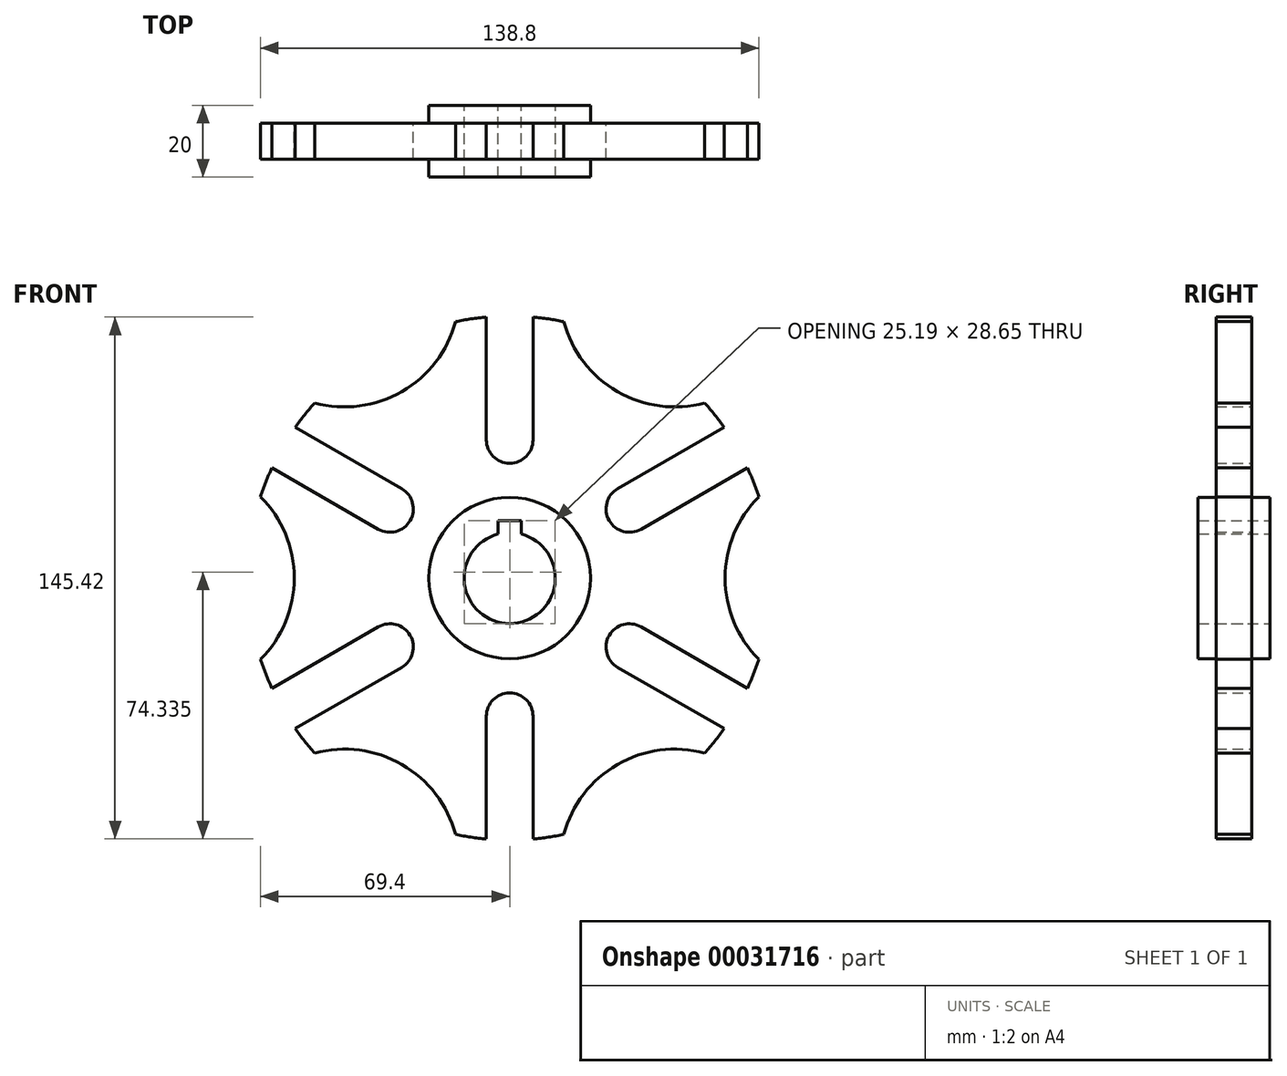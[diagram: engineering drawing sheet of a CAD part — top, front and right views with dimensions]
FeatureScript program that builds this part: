
annotation { "Feature Type Name" : "Feature", "Feature Type Description" : "" }
export const myFeature = defineFeature(function(context is Context, id is Id, definition is map)
    precondition{}
    {
        {
            var Q0;
            Q0=qCreatedBy(makeId("Front.planeOp"),FACE);
            var sketch = newSketch(context, id + "F0", { "sketchPlane" : qUnion([Q0])});
            skCircle(sketch, "E0", {"center": v(0, 0) * mm, "radius": 22.5 * mm});
            skCircle(sketch, "E1", {"center": v(0, 0) * mm, "radius": 12.7 * mm});
            skLineSegment(sketch, "E2", {"start": v(0, 12.7) * mm, "end": v(0, 15.95) * mm});
            skLineSegment(sketch, "E3", {"start": v(0, 15.95) * mm, "end": v(3.25, 15.95) * mm});
            skLineSegment(sketch, "E4", {"start": v(3.25, 15.95) * mm, "end": v(3.25, 12.28) * mm});
            skLineSegment(sketch, "E5", {"start": v(0, 15.95) * mm, "end": v(-3.25, 15.95) * mm});
            skLineSegment(sketch, "E6", {"start": v(-3.25, 15.95) * mm, "end": v(-3.25, 12.28) * mm});
            skSolve(sketch);
        }
        {
            var Q0;
            Q0=makeQuery(id+"F0.imprint","IMPRINT",FACE,{"disambiguationData":[TD([[makeQuery(id+"F0.imprint","IMPRINT",EDGE,{"derivedFrom":sQuery(id+"F0.wireOp",EDGE,"E0")}),1.0]])]});
            extrude(context, id + "F1", {"entities" : qUnion([Q0]), "endBound" : BoundingType.SYMMETRIC, "depth" : 20 * mm});
        }
        {
            var Q0;
            Q0=qCreatedBy(makeId("Front.planeOp"),FACE);
            var sketch = newSketch(context, id + "F2", { "sketchPlane" : qUnion([Q0])});
            skCircle(sketch, "E7", {"center": v(0, 0) * mm, "radius": 73 * mm});
            skCircle(sketch, "E8", {"center": v(0, 0) * mm, "radius": 22.5 * mm});
            skCircle(sketch, "E9", {"center": v(0, 0) * mm, "radius": 38.5 * mm, "construction": true});
            skArc(sketch, "E10", {"start": v(-6.5, 38.5) * mm, "mid": v(0, 32) * mm, "end": v(6.5, 38.5) * mm});
            skLineSegment(sketch, "E11", {"start": v(-6.5, 38.5) * mm, "end": v(-6.5, 72.71) * mm});
            skLineSegment(sketch, "E12", {"start": v(6.5, 38.5) * mm, "end": v(6.5, 72.71) * mm});
            skLineSegment(sketch, "E13.1.0", {"start": v(-30.1, 24.88) * mm, "end": v(-59.72, 41.98) * mm});
            skArc(sketch, "E13.1.1", {"start": v(-36.6, 13.62) * mm, "mid": v(-27.71, 16) * mm, "end": v(-30.1, 24.88) * mm});
            skLineSegment(sketch, "E13.1.2", {"start": v(-36.6, 13.62) * mm, "end": v(-66.22, 30.73) * mm});
            skLineSegment(sketch, "E13.2.0", {"start": v(-36.6, -13.62) * mm, "end": v(-66.22, -30.73) * mm});
            skArc(sketch, "E13.2.1", {"start": v(-30.1, -24.88) * mm, "mid": v(-27.71, -16) * mm, "end": v(-36.6, -13.62) * mm});
            skLineSegment(sketch, "E13.2.2", {"start": v(-30.1, -24.88) * mm, "end": v(-59.72, -41.98) * mm});
            skLineSegment(sketch, "E14.1.3.0", {"start": v(-6.5, -38.5) * mm, "end": v(-6.5, -72.71) * mm});
            skArc(sketch, "E14.3.3.0", {"start": v(6.5, -38.5) * mm, "mid": v(0, -32) * mm, "end": v(-6.5, -38.5) * mm});
            skLineSegment(sketch, "E14.7.3.0", {"start": v(6.5, -38.5) * mm, "end": v(6.5, -72.71) * mm});
            skLineSegment(sketch, "E14.1.4.0", {"start": v(30.1, -24.88) * mm, "end": v(59.72, -41.98) * mm});
            skArc(sketch, "E14.3.4.0", {"start": v(36.6, -13.62) * mm, "mid": v(27.71, -16) * mm, "end": v(30.1, -24.88) * mm});
            skLineSegment(sketch, "E14.7.4.0", {"start": v(36.6, -13.62) * mm, "end": v(66.22, -30.73) * mm});
            skLineSegment(sketch, "E14.1.5.0", {"start": v(36.6, 13.62) * mm, "end": v(66.22, 30.73) * mm});
            skArc(sketch, "E14.3.5.0", {"start": v(30.1, 24.88) * mm, "mid": v(27.71, 16) * mm, "end": v(36.6, 13.62) * mm});
            skLineSegment(sketch, "E14.7.5.0", {"start": v(30.1, 24.88) * mm, "end": v(59.72, 41.98) * mm});
            skArc(sketch, "E15", {"start": v(69.4, 22.65) * mm, "mid": v(60, 0) * mm, "end": v(69.4, -22.65) * mm});
            skArc(sketch, "E16.1.0", {"start": v(15.08, 71.43) * mm, "mid": v(30, 51.96) * mm, "end": v(54.32, 48.77) * mm});
            skArc(sketch, "E16.2.0", {"start": v(-54.32, 48.77) * mm, "mid": v(-30, 51.96) * mm, "end": v(-15.08, 71.43) * mm});
            skArc(sketch, "E16.3.0", {"start": v(-69.4, -22.65) * mm, "mid": v(-60, 0) * mm, "end": v(-69.4, 22.65) * mm});
            skArc(sketch, "E16.4.0", {"start": v(-15.08, -71.43) * mm, "mid": v(-30, -51.96) * mm, "end": v(-54.32, -48.77) * mm});
            skArc(sketch, "E16.5.0", {"start": v(54.32, -48.77) * mm, "mid": v(30, -51.96) * mm, "end": v(15.08, -71.43) * mm});
            skSolve(sketch);
        }
        {
            var Q0;
            Q0=makeQuery(id+"F2.imprint","IMPRINT",FACE,{"disambiguationData":[TD([[makeQuery(id+"F2.imprint","IMPRINT",EDGE,{"derivedFrom":sQuery(id+"F2.wireOp",EDGE,"E8")}),-1.0]])]});
            extrude(context, id + "F3", {"entities" : qUnion([Q0]), "operationType" : NewBodyOperationType.ADD, "endBound" : BoundingType.SYMMETRIC, "depth" : 10 * mm});
        }
    });
